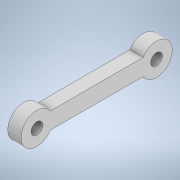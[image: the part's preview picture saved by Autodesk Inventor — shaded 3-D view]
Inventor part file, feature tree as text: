
AUTODESK INVENTOR PART (.ipt)
format: ipt  version: 2020 (Build 240168000, 168)  size: 122,880 bytes
history: native  units: in
note: dims shown in document units (in); Inventor stores cm internally (conversion verified against a paired STEP export)
features: extrude x1, sketch x1
ambient origin geometry x8: Origin, YZ Plane, XZ Plane, XY Plane, X Axis, Y Axis, Z Axis, Center Point
bodies: Solid1 (feature_tree)
feature tree (2):
  extrude  "Extrusion1"  Depth=1.4173in
  sketch  "Sketch1"  dims[d0=0.1378in d1=1.4173in d2=0.1181in d3=0.1181in d4=0.1969in d5=0.1575in d6=0.0in]
